# Revit family: Baies Linkeo avec porte avant double largeur 800
name_source: partatom
category: Equipement spécialisé
units: mm (PartAtom-declared; Revit-internal decimal feet)

## family parameters
Basée sur le plan de construction = Non
Cote de connecteur circulaire = Utiliser le diamètre
Couper avec des vides une fois chargée = Non
Numéro OmniClass = 23.85.05.17.11.14
Partagée = Oui
Point de calcul de pièce = Non
Titre OmniClass = Multimedia Broadcasting Equipment
Toujours verticalement = Oui
Type d'élément = Normal

## types (3) — shared parameters
Avec mise à la terre = Oui
Avec porte frontale = Oui
Avec tôle de toit = Oui
Capacité de charge max = 400
Classe d'application = EC002499
Couleur = gris
Dimension modulaire = 19 pouces
Emplacement de rack = 93 mm  [stored 0.305118 ft]
Finition de surface = Poudré
Finition du rail profilé = Recourbée
Fonction = Baie Linkeo2
Hauteur = 2026 mm  [stored 6.64698 ft]
Indice de protection IK = IK08
Indice de protection IP = IP20
Largeur (mm) = 810 mm
Lien e-catalogue = https://www.legrand.fr
Matériau = Acier
Matériau de la porte avant = Verre
Modèle = Corps fixe
Modèle de largeur = 800 mm  [stored 2.62467 ft]
Nombre d'unités en hauteur = 42
Nombre de portes = 2
RAL = 7016
Température de fonctionnement = -25°C à 70°C
Température de stockage = -25°C à 70°C
Type d'aération = Aucune
Type de montage = Frontal
Type de montants verticaux = Montants verticaux pour armoires Linkeo  42U
Verrouillage de la porte avant = A un point
zero-valued in all types: Elévation par défaut

## per-type parameters (varying)
| type | Distance ouverture 1 | Distance ouverture 2 | EAN | Passage utile en hauteur (mm) | Passage utile en largeur (mm) | Profondeur | Profondeur du modèle | Référence Legrand | Type de montants horizontaux | Type de pieds de nivellement |
| Baie Linkeo2 42U 800x600 double porte | 57 mm  [stored 0.187008 ft] | 98 mm  [stored 0.321522 ft] | 3414971001602 | 1786 mm  [stored 5.85958 ft] | 490 mm  [stored 1.60761 ft] | 630 mm  [stored 2.06693 ft] | 600 mm | 646766 | Montants horizontaux pour armoires Linkeo  42U profondeur 600 | Pieds de nivellement  800X600 |
| Baie Linkeo2 42U 800x800 double porte | 257 mm  [stored 0.843176 ft] | 198 mm  [stored 0.649606 ft] | 3414971001619 | 1786 mm  [stored 5.85958 ft] | 690 mm  [stored 2.26378 ft] | 830 mm  [stored 2.7231 ft] | 800 mm  [stored 2.62467 ft] | 646767 | Montants horizontaux pour armoires Linkeo  42U profondeur 800 | Pieds de nivellement  800X800 |
| Baie Linkeo2 42U 800x1000 double porte | 457 mm  [stored 1.49934 ft] | 298 mm  [stored 0.97769 ft] | 3414971001626 | 1881 mm  [stored 6.17126 ft] | 890 mm  [stored 2.91995 ft] | 1030 mm  [stored 3.37927 ft] | 1000 mm  [stored 3.28084 ft] | 646768 | Montants horizontaux pour armoires Linkeo  42U profondeur 1000 | Pieds de nivellement  800X1000 |

note: column(s) folded — value = type name in every type: Libellé BIM

note: [stored X ft] marks values corroborated as IEEE doubles in the binary element streams (Revit-internal decimal feet)
